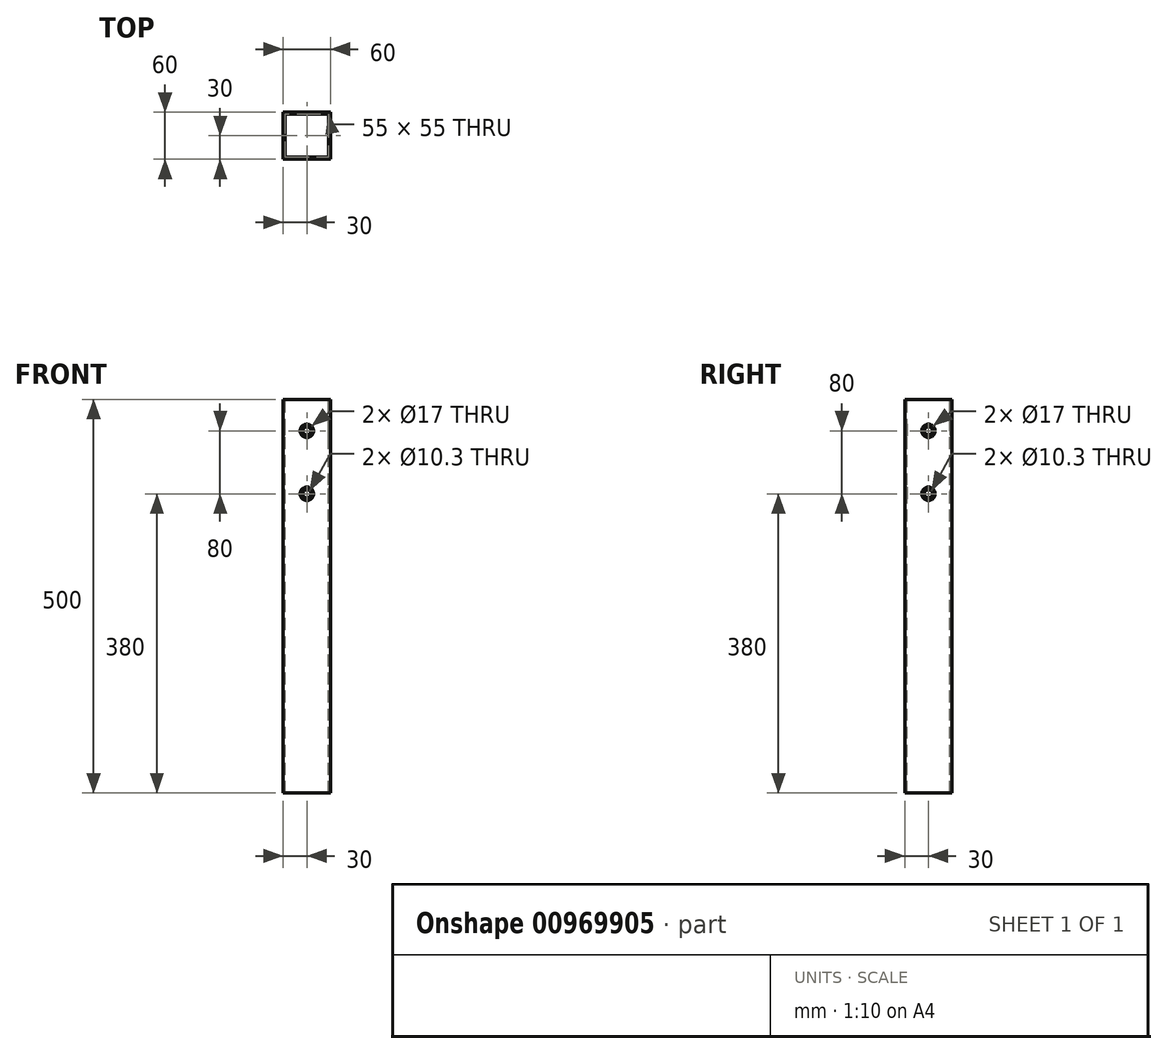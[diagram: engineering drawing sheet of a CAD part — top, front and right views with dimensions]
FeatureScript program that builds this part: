
annotation { "Feature Type Name" : "Feature", "Feature Type Description" : "" }
export const myFeature = defineFeature(function(context is Context, id is Id, definition is map)
    precondition{}
    {
        {
            var Q0;
            Q0=qCreatedBy(makeId("Top.planeOp"),FACE);
            var sketch = newSketch(context, id + "F0", { "sketchPlane" : qUnion([Q0])});
            skLineSegment(sketch, "E0.bottom", {"start": v(27.5, -27.5) * mm, "end": v(-27.5, -27.5) * mm});
            skLineSegment(sketch, "E0.top", {"start": v(27.5, 27.5) * mm, "end": v(-27.5, 27.5) * mm});
            skLineSegment(sketch, "E0.left", {"start": v(27.5, -27.5) * mm, "end": v(27.5, 27.5) * mm});
            skLineSegment(sketch, "E0.right", {"start": v(-27.5, -27.5) * mm, "end": v(-27.5, 27.5) * mm});
            skPoint(sketch, "E0.middle", {"position": v(0, 0) * mm});
            skLineSegment(sketch, "E1.bottom", {"start": v(30, -30) * mm, "end": v(-30, -30) * mm});
            skLineSegment(sketch, "E1.top", {"start": v(30, 30) * mm, "end": v(-30, 30) * mm});
            skLineSegment(sketch, "E1.left", {"start": v(30, -30) * mm, "end": v(30, 30) * mm});
            skLineSegment(sketch, "E1.right", {"start": v(-30, -30) * mm, "end": v(-30, 30) * mm});
            skSolve(sketch);
        }
        {
            var Q0;
            Q0=makeQuery(id+"F0.imprint","IMPRINT",FACE,{"disambiguationData":[TD([[makeQuery(id+"F0.imprint","IMPRINT",EDGE,{"derivedFrom":sQuery(id+"F0.wireOp",EDGE,"E0.bottom")}),1.0]])]});
            extrude(context, id + "F1", {"entities" : qUnion([Q0]), "oppositeDirection" : true, "depth" : 500 * mm, "offsetDistance" : 25 * mm});
        }
        {
            var Q0;
            Q0=makeQuery(id+"F1.opExtrude","SWEPT_FACE",FACE,{"disambiguationData":[OSD([sQuery(id+"F0.wireOp",EDGE,"E1.bottom")])]});
            var sketch = newSketch(context, id + "F2", { "sketchPlane" : qUnion([Q0])});
            skLineSegment(sketch, "E2", {"start": v(0, 0) * mm, "end": v(0, -500) * mm, "construction": true});
            skCircle(sketch, "E3", {"center": v(0, -40) * mm, "radius": 8.5 * mm});
            skCircle(sketch, "E4", {"center": v(0, -120) * mm, "radius": 8.5 * mm});
            skSolve(sketch);
        }
        {
            var Q0;
            Q0=makeQuery(id+"F2.imprint","IMPRINT",FACE,{"disambiguationData":[TD([[makeQuery(id+"F2.imprint","IMPRINT",EDGE,{"derivedFrom":sQuery(id+"F2.wireOp",EDGE,"E3")}),1.0]])]});
            var Q1;
            Q1=makeQuery(id+"F2.imprint","IMPRINT",FACE,{"disambiguationData":[TD([[makeQuery(id+"F2.imprint","IMPRINT",EDGE,{"derivedFrom":sQuery(id+"F2.wireOp",EDGE,"E4")}),1.0]])]});
            extrude(context, id + "F3", {"entities" : qUnion([Q0, Q1]), "operationType" : NewBodyOperationType.REMOVE, "oppositeDirection" : true, "depth" : 5 * mm, "offsetDistance" : 25 * mm});
        }
        {
            var Q0;
            Q0=makeQuery(id+"F1.opExtrude","SWEPT_FACE",FACE,{"disambiguationData":[OSD([sQuery(id+"F0.wireOp",EDGE,"E1.left")])]});
            var sketch = newSketch(context, id + "F4", { "sketchPlane" : qUnion([Q0])});
            skLineSegment(sketch, "E5", {"start": v(0, 0) * mm, "end": v(0, -500) * mm, "construction": true});
            skCircle(sketch, "E6", {"center": v(0, -40) * mm, "radius": 8.5 * mm});
            skCircle(sketch, "E7", {"center": v(0, -120) * mm, "radius": 8.5 * mm});
            skSolve(sketch);
        }
        {
            var Q0;
            Q0=makeQuery(id+"F4.imprint","IMPRINT",FACE,{"disambiguationData":[TD([[makeQuery(id+"F4.imprint","IMPRINT",EDGE,{"derivedFrom":sQuery(id+"F4.wireOp",EDGE,"E6")}),1.0]])]});
            var Q1;
            Q1=makeQuery(id+"F4.imprint","IMPRINT",FACE,{"disambiguationData":[TD([[makeQuery(id+"F4.imprint","IMPRINT",EDGE,{"derivedFrom":sQuery(id+"F4.wireOp",EDGE,"E7")}),1.0]])]});
            extrude(context, id + "F5", {"entities" : qUnion([Q0, Q1]), "operationType" : NewBodyOperationType.REMOVE, "oppositeDirection" : true, "depth" : 5 * mm, "offsetDistance" : 25 * mm});
        }
        {
            var Q0;
            Q0=makeQuery(id+"F1.opExtrude","SWEPT_FACE",FACE,{"disambiguationData":[OSD([sQuery(id+"F0.wireOp",EDGE,"E1.top")])]});
            var sketch = newSketch(context, id + "F6", { "sketchPlane" : qUnion([Q0])});
            skLineSegment(sketch, "E8", {"start": v(0, 0) * mm, "end": v(0, -500) * mm, "construction": true});
            skCircle(sketch, "E9", {"center": v(0, -40) * mm, "radius": 5.15 * mm});
            skCircle(sketch, "E10", {"center": v(0, -120) * mm, "radius": 5.15 * mm});
            skSolve(sketch);
        }
        {
            var Q0;
            Q0=makeQuery(id+"F6.imprint","IMPRINT",FACE,{"disambiguationData":[TD([[makeQuery(id+"F6.imprint","IMPRINT",EDGE,{"derivedFrom":sQuery(id+"F6.wireOp",EDGE,"E9")}),1.0]])]});
            var Q1;
            Q1=makeQuery(id+"F6.imprint","IMPRINT",FACE,{"disambiguationData":[TD([[makeQuery(id+"F6.imprint","IMPRINT",EDGE,{"derivedFrom":sQuery(id+"F6.wireOp",EDGE,"E10")}),1.0]])]});
            extrude(context, id + "F7", {"entities" : qUnion([Q0, Q1]), "operationType" : NewBodyOperationType.REMOVE, "oppositeDirection" : true, "depth" : 5 * mm, "offsetDistance" : 25 * mm});
        }
        {
            var Q0;
            Q0=makeQuery(id+"F1.opExtrude","SWEPT_FACE",FACE,{"disambiguationData":[OSD([sQuery(id+"F0.wireOp",EDGE,"E1.right")])]});
            var sketch = newSketch(context, id + "F8", { "sketchPlane" : qUnion([Q0])});
            skLineSegment(sketch, "E11", {"start": v(0, 0) * mm, "end": v(0, -500) * mm, "construction": true});
            skCircle(sketch, "E12", {"center": v(0, -40) * mm, "radius": 5.15 * mm});
            skCircle(sketch, "E13", {"center": v(0, -120) * mm, "radius": 5.15 * mm});
            skSolve(sketch);
        }
        {
            var Q0;
            Q0=makeQuery(id+"F8.imprint","IMPRINT",FACE,{"disambiguationData":[TD([[makeQuery(id+"F8.imprint","IMPRINT",EDGE,{"derivedFrom":sQuery(id+"F8.wireOp",EDGE,"E12")}),1.0]])]});
            var Q1;
            Q1=makeQuery(id+"F8.imprint","IMPRINT",FACE,{"disambiguationData":[TD([[makeQuery(id+"F8.imprint","IMPRINT",EDGE,{"derivedFrom":sQuery(id+"F8.wireOp",EDGE,"E13")}),1.0]])]});
            extrude(context, id + "F9", {"entities" : qUnion([Q0, Q1]), "operationType" : NewBodyOperationType.REMOVE, "oppositeDirection" : true, "depth" : 5 * mm, "offsetDistance" : 25 * mm});
        }
    });
